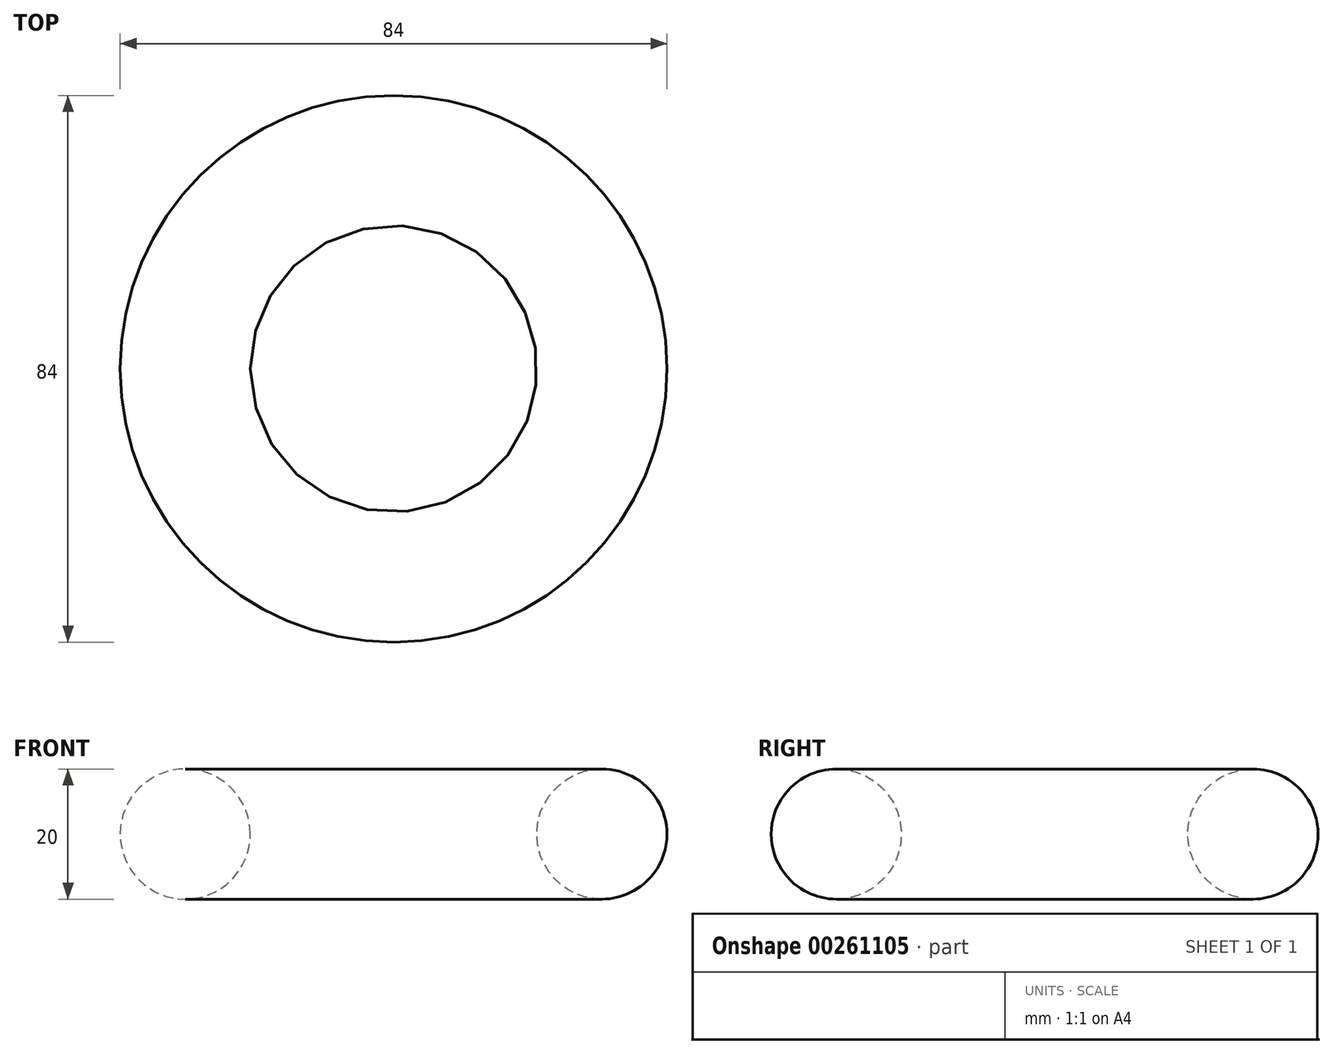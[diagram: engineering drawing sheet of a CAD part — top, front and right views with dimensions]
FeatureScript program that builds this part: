
annotation { "Feature Type Name" : "Feature", "Feature Type Description" : "" }
export const myFeature = defineFeature(function(context is Context, id is Id, definition is map)
    precondition{}
    {
        {
            var Q0;
            Q0=qCreatedBy(makeId("Front.planeOp"),FACE);
            var sketch = newSketch(context, id + "F0", { "sketchPlane" : qUnion([Q0])});
            skCircle(sketch, "E0", {"center": v(32, 0) * mm, "radius": 10 * mm});
            skLineSegment(sketch, "E1", {"start": v(0, 30.15) * mm, "end": v(0, -51.92) * mm, "construction": true});
            skSolve(sketch);
        }
        {
            var Q0;
            Q0=sQuery(id+"F0.wireOp",EDGE,"E0");
            var Q1;
            Q1=sQuery(id+"F0.wireOp",EDGE,"E1");
            revolve(context, id + "F1", {"bodyType" : ToolBodyType.SURFACE, "surfaceEntities" : qUnion([Q0]), "axis" : qUnion([Q1]), "revolveType" : RevolveType.FULL});
        }
    });
